# Revit family: RA-IN_Double Angle_Right_DN10-15_Aveo_RFA
name_source: partatom
category: Pipe Accessories
units: mm (PartAtom-declared; Revit-internal decimal feet)

## family parameters
Always vertical = Yes
Cut with Voids When Loaded = No
OmniClass Number = 23.65.55.14.17
OmniClass Title = Adjusting/Controlling Valves for Liquid Services
Part Type = Valve - Breaks Into
Round Connector Dimension = Use Diameter
Shared = No
Work Plane-Based = No

## types (2) — shared parameters
Connection = Internal thread
DB4 = 25.6 mm  [stored 0.0839895 ft]
Description = Thermostatic Radiator Valve
H1 = 15 mm  [stored 0.0492126 ft]
HH = 22 mm  [stored 0.0721785 ft]
HT = 99 mm  [stored 0.324803 ft]
IfcExportAs = IfcValveType
IfcExportType = RA-IN
L2 = 4 mm  [stored 0.0131234 ft]
L3 = 6 mm  [stored 0.019685 ft]
LOD 200 = No
LOD 350 = Yes
Manufacturer = Danfoss
Max Differential Pressure = 0.6 bar
Max Medium Temperature = 120 ˚C
Max Operating Pressure = 10 bar
SH = 33 mm  [stored 0.108268 ft]
Sensor Type = Aveo Sensors_RA_RFA : Aveo Sensors_Built-in_7-28 °C
Setting Range = 1-4,N
Tamp_Built-in = Aveo Sensors_RA_RFA : Aveo Sensors_Tamperproof_Built-in_7-28 °C
Tamp_Remote = Aveo Sensors_RA_RFA : Aveo Sensors_Tamperproof_Remote_7-26 °C_015G4042
URL = https://store.danfoss.com
Valve Body Material = Danfoss Brass (Nickel plated)
Wa = 28 mm  [stored 0.0918635 ft]

## per-type parameters (varying)
- RA-IN_Double Angle_Right_DN10_013G6571: D=10 mm  [stored 0.0328084 ft]; H=114.5 mm; Kvs=0.7 m³/h; L=80 mm  [stored 0.262467 ft]; L1=15 mm  [stored 0.0492126 ft]; L4=8.5 mm  [stored 0.0278871 ft]; L5=27 mm  [stored 0.0885827 ft]; L6=16 mm  [stored 0.0524934 ft]; LL=52 mm; L_nut thread1=22 mm  [stored 0.0721785 ft]; L_nut thread2=27 mm  [stored 0.0885827 ft]; Model=013G6571; Model Type=RA-IN_Double Angle_Right_DN10; RB=12.8 mm  [stored 0.0419948 ft]; RB2=10.5 mm  [stored 0.0344488 ft]; RB3=10.5 mm  [stored 0.0344488 ft]; RV1=10.5 mm  [stored 0.0344488 ft]; RV1_1=10 mm  [stored 0.0328084 ft]; RV2=10 mm  [stored 0.0328084 ft]; RV3=13.3 mm  [stored 0.0436352 ft]; RV4=8.3 mm  [stored 0.027231 ft]; R_200=12.7 mm  [stored 0.0416667 ft]; R_200_1=15.5 mm  [stored 0.050853 ft]; SL=33.5 mm; W=55 mm  [stored 0.180446 ft]; Weight=0.23 kg
- RA-IN_Double Angle_Right_DN15_013G6573: D=15 mm  [stored 0.0492126 ft]; H=116.32 mm; Kvs=0.9 m³/h; L=86 mm  [stored 0.282152 ft]; L1=17 mm; L4=10 mm  [stored 0.0328084 ft]; L5=33 mm  [stored 0.108268 ft]; L6=17 mm; LL=58 mm  [stored 0.190289 ft]; L_nut thread1=27 mm  [stored 0.0885827 ft]; L_nut thread2=30 mm  [stored 0.0984252 ft]; Model=013G6573; Model Type=RA-IN_Double Angle_Right_DN15; RB=15.5 mm  [stored 0.050853 ft]; RB2=13 mm; RB3=1 mm  [stored 0.00328084 ft]; RV1=13 mm; RV1_1=11.5 mm  [stored 0.0377297 ft]; RV2=11.5 mm  [stored 0.0377297 ft]; RV3=14.8 mm  [stored 0.0485564 ft]; RV4=10.5 mm  [stored 0.0344488 ft]; R_200=15.5 mm  [stored 0.050853 ft]; R_200_1=17.32 mm; SL=37 mm; W=61 mm  [stored 0.200131 ft]; Weight=0.30 kg

note: [stored X ft] marks values corroborated as IEEE doubles in the binary element streams (Revit-internal decimal feet)

## geometry (parser evidence)
native form markers: Sweep x12
no freeform markers — native parametric forms only
